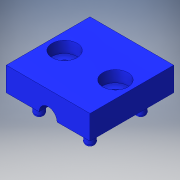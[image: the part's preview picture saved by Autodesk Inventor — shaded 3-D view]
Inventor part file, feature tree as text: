
AUTODESK INVENTOR PART (.ipt)
format: ipt  version: 2016 SP1 (Build 200210100, 210)  size: 162,304 bytes
history: native  units: in
note: dims shown in document units (in); Inventor stores cm internally (conversion verified against a paired STEP export)
features: sketch x5, hole x3, extrude x2, fillet x1
ambient origin geometry x8: Origin, YZ Plane, XZ Plane, XY Plane, X Axis, Y Axis, Z Axis, Center Point
bodies: Body1 (feature_tree)
feature tree (11):
  extrude  "Extrusion3"  Depth=1.75in
  hole  "Hole2"  [1 undecoded]
  hole  "Hole3"  [1 undecoded]
  hole  "Hole4"  [1 undecoded]
  extrude  "Extrusion4"  Depth=0.0625in
  fillet  "Fillet1"  Radius=0.3438in
  sketch  "Sketch5"  dims[d0=1.75in d1=0.4375in]
  sketch  "Sketch6"  dims[d2=0.0in d3=0.375in]
  sketch  "Sketch7"  dims[d5=0.0in d23=1.75in]
  sketch  "Sketch8"  dims[d24=0.5in d25=0.0in]
  sketch  "Sketch9"  dims[d26=0.375in d27=0.75in d28=0.375in d29=0.25in d30=0.5635in d31=1.0in d32=0.8108in d33=0.3438in d34=0.3438in d35=0.525in d36=0.75in d37=0.375in d38=0.25in d39=0.5635in d40=0.24in d41=0.0in d42=0.3438in d43=0.3438in d44=0.201in d45=0.75in d46=0.385in d47=0.25in d48=0.5635in d49=1.0in d50=0.8108in d51=0.875in d52=0.875in d53=0.875in d54=0.875in d55=0.3438in d56=0.3438in d57=0.2in d58=0.4in d59=0.0in d60=0.0625in]
note: 3 required parameter values undecoded (feature->parameter linkage not recoverable at this tier; creation-order binding heuristic only, values carry confidence <= 0.55)
